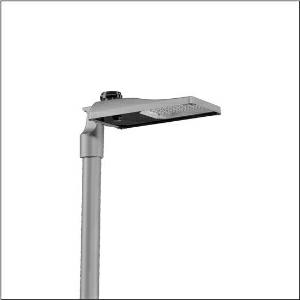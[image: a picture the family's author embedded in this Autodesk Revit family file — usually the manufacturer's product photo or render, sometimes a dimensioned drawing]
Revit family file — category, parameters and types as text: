
# Revit family: streetlight_sl_31_mini___st1_0a_5xh2d3bm08ja_c740
name_source: partatom
category: Lighting Fixtures
units: mm (PartAtom-declared; Revit-internal decimal feet)

## family parameters
Cut with Voids When Loaded = No
Host = Face
Light Source = No
Part Type = Normal
Room Calculation Point = No
Round Connector Dimension = Use Diameter
Shared = No

## types (1)
- --- (1 x LED, 12270 lm, 82.5 W, 3000K)
    Apparent Load = 83 VA
    CIE Flux Codes = 40 73 97 100 100
    Color Rendering = 70
    Color Temperature = 3000K
    Default Elevation = 1800 mm
    Description = Streetlight SL 31 mini NEMA (7pin) mast luminaire for post-top, side-entry; light control with lens of PMMA; light distribution: ST1.0a, direct asymmetric distribution, for standard-compliant lighting for roads and squares; LED: luminous flux: 12.270lm, light colour: 730, colour temperature: 3000K; luminous efficacy: 148,7lm/W; control: pre-setting: linear dimming characteristic, flexible luminous flux parameterisation, time-dependent luminous flux control, constant luminous flux control, intelligent temperature release in ECG and LED module, overheat protection; luminaire housing, of diecast aluminium, Siteco® metallic grey (DB 702S), corrosivity category C5 high according to DIN EN ISO 12944; cover of toughened safety glass, transparent, mast flange of diecast aluminium, Siteco® metallic grey (DB 702S), spigot size: 76/60mm, mast flange included unmounted; with cable H07RN-F 3x 1.5mm², cable length: 10,5m, connection cable pre-assembled; mains connection: 220..240V, AC, 50/60Hz; power consumption (at start of service life): 82,5W / (at end of service life): 90,1W / (with reduced operation 50%): 36,8W; protection rating (complete): IP66; insulation class (complete): insulation class I (protective earthing); impact resistance: IK09; certification: CE, ENEC, ENEC+, VDE, UKCA; permissible operating ambient temperature for outdoor applications: -40..+50°C; packaging unit: 1 piece

Light Distribution: ST1.0a
    Height = 76 mm
    Lamp = 1 x LED
    Lamp Light Flux = 12270 lm
    Lamp Power = 82.5 W
    Lamp count = 1
    Length = 547 mm
    Luminous efficacy = 149 lm/W
    Manufacturer = Siteco
    ModVariant = No
    Model = 5XH2D3BM08JA
    Number of Poles = 1
    OnlyDefault = Yes
    Power Factor = 1
    Product Name = Streetlight SL 31 mini | ST1.0a
    Product group = mast luminaire | pylon top
    ProductGroupID = 6100
    Protection Class = Protection class I
    Protection Degree = IP 66
    RLX_Detail_Level = 1
    RLX_Emergency_Light_Flux = 0 lm
    RLX_Emergency_Type = 0
    RLX_Emergency_Type_DB = No
    RlxData = <blob elided: 40233 chars, md5=d6788d46>
    Socket = socket
    Standby Power = 0 W
    System Light Flux = 12270 lm
    System Power = 83 W
    Type Comments = factory setting: luminous flux: 100 % | dim-lin: 254 | 870 mA
    Type Image = l_1300324.jpg
    URL = http://relux.com
    VarID = @adj_047494
    Voltage = 0 V
    Weight = 0.00 kg
    Width = 265 mm

## geometry (parser evidence)
native form markers: Blend x4, Sweep x9
no freeform markers — native parametric forms only
